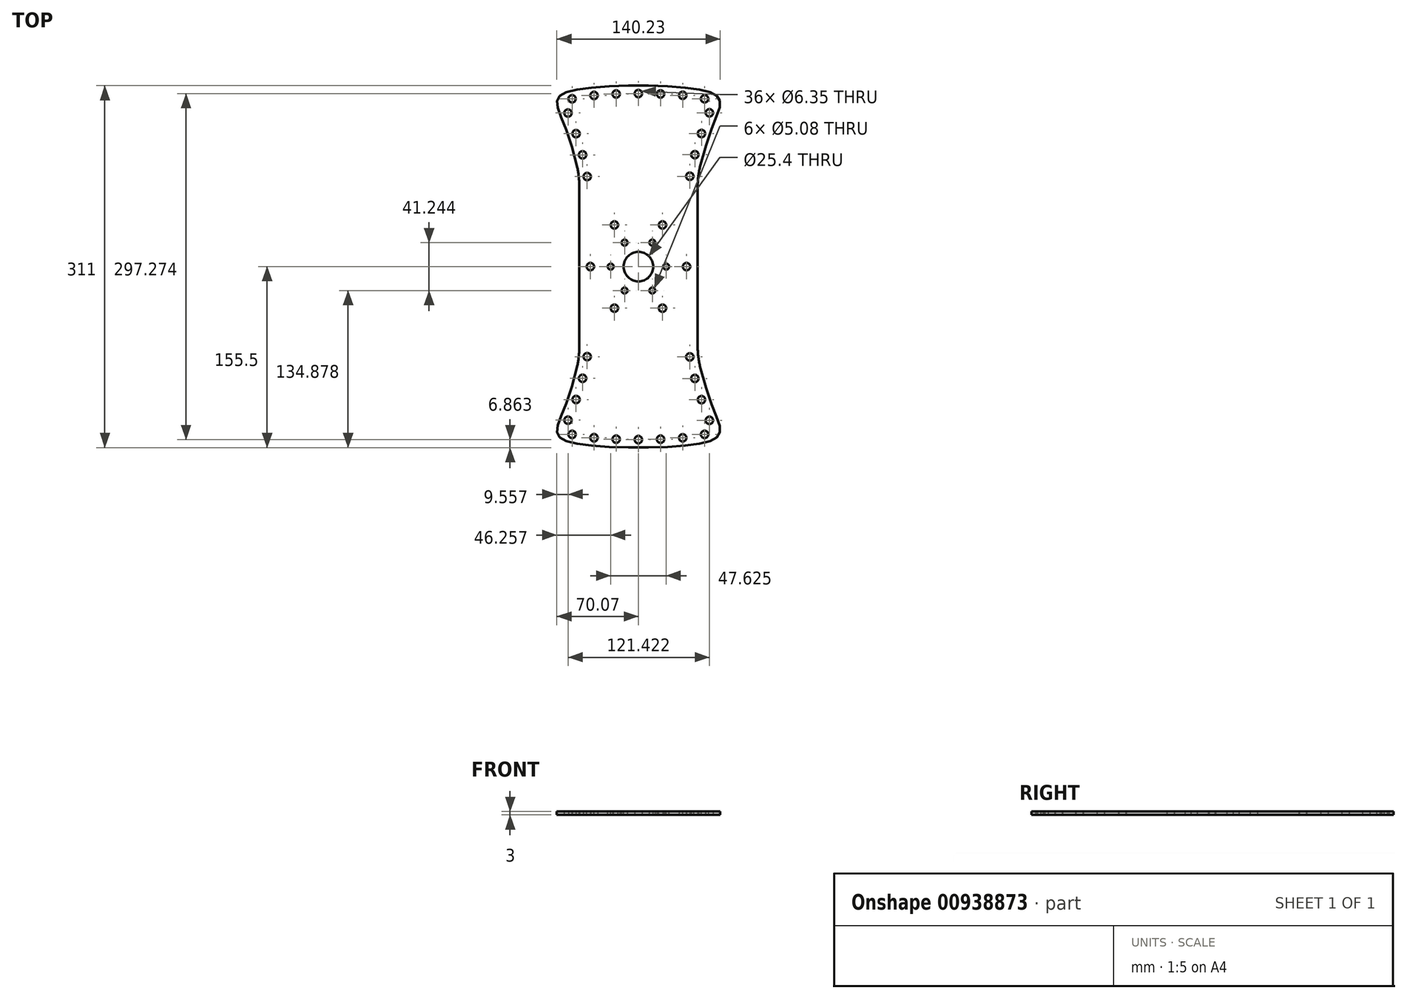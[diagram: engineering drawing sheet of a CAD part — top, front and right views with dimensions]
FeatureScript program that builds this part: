
annotation { "Feature Type Name" : "Feature", "Feature Type Description" : "" }
export const myFeature = defineFeature(function(context is Context, id is Id, definition is map)
    precondition{}
    {
        {
            var Q0;
            Q0=qCreatedBy(makeId("Top.planeOp"),FACE);
            var sketch = newSketch(context, id + "F0", { "sketchPlane" : qUnion([Q0])});
            skArc(sketch, "E0", {"start": v(-50.8, 0) * mm, "mid": v(0, -50.8) * mm, "end": v(50.8, 0) * mm});
            skLineSegment(sketch, "E1", {"start": v(-50.8, 0) * mm, "end": v(-50.8, 69.13) * mm});
            skLineSegment(sketch, "E2", {"start": v(50.8, 0) * mm, "end": v(50.8, 68.08) * mm});
            skFitSpline(sketch, "E3", {"points": [v(-50.8, 76.2) * mm, v(-69.85, 142.88) * mm, v(-50.8, 152.4) * mm, v(50.8, 152.4) * mm, v(69.85, 142.88) * mm, v(50.8, 76.2) * mm], "startDerivative": vector(-90.93, 536.28) * mm, "endDerivative": vector(-110.86, -555.74) * mm});
            skFitSpline(sketch, "E4.0", {"points": [v(-44.04, 77.35) * mm, v(-45.01, 83.1) * mm, v(-47.24, 93.68) * mm, v(-51.03, 107.03) * mm, v(-54.92, 118.08) * mm, v(-57.9, 125.53) * mm, v(-59.94, 130.5) * mm, v(-61.23, 133.73) * mm, v(-62.23, 136.46) * mm, v(-62.9, 138.66) * mm, v(-63.15, 139.98) * mm, v(-63.22, 140.7) * mm, v(-63.22, 141.05) * mm, v(-63.2, 141.23) * mm, v(-63.18, 141.28) * mm, v(-63.18, 141.28) * mm, v(-63.17, 141.3) * mm, v(-63.13, 141.35) * mm, v(-62.98, 141.54) * mm, v(-62.48, 141.96) * mm, v(-61.24, 142.67) * mm, v(-59.33, 143.45) * mm, v(-56.79, 144.22) * mm, v(-53.64, 144.94) * mm, v(-49.93, 145.62) * mm, v(-45.67, 146.24) * mm, v(-40.94, 146.79) * mm, v(-34.1, 147.44) * mm, v(-24.7, 148.07) * mm, v(-12.54, 148.53) * mm, v(0.06, 148.69) * mm, v(12.66, 148.54) * mm, v(24.8, 148.1) * mm, v(34.17, 147.47) * mm, v(40.97, 146.82) * mm, v(45.67, 146.25) * mm, v(49.9, 145.62) * mm, v(53.57, 144.93) * mm, v(56.68, 144.19) * mm, v(59.2, 143.4) * mm, v(61.1, 142.6) * mm, v(62.38, 141.88) * mm, v(62.93, 141.42) * mm, v(63.14, 141.19) * mm, v(63.21, 141.08) * mm, v(63.24, 141.03) * mm, v(63.25, 141) * mm, v(63.27, 140.95) * mm, v(63.3, 140.8) * mm, v(63.3, 140.5) * mm, v(63.28, 139.88) * mm, v(63.1, 138.7) * mm, v(62.54, 136.65) * mm, v(61.65, 134.06) * mm, v(60.48, 130.96) * mm, v(58.57, 126.14) * mm, v(55.7, 118.82) * mm, v(51.8, 107.8) * mm, v(47.79, 94.3) * mm, v(45.26, 83.47) * mm, v(44.07, 77.54) * mm]});
            skCircle(sketch, "E5", {"center": v(-56.97, 144.13) * mm, "radius": 3.18 * mm});
            skCircle(sketch, "E6", {"center": v(-38.15, 147.05) * mm, "radius": 3.18 * mm});
            skCircle(sketch, "E7", {"center": v(-19.13, 148.26) * mm, "radius": 3.18 * mm});
            skCircle(sketch, "E8", {"center": v(-0.08, 148.64) * mm, "radius": 3.18 * mm});
            skCircle(sketch, "E9", {"center": v(18.96, 148.3) * mm, "radius": 3.18 * mm});
            skCircle(sketch, "E10", {"center": v(37.98, 147.1) * mm, "radius": 3.18 * mm});
            skCircle(sketch, "E11", {"center": v(56.8, 144.12) * mm, "radius": 3.18 * mm});
            skCircle(sketch, "E12", {"center": v(-60.51, 131.94) * mm, "radius": 3.18 * mm});
            skCircle(sketch, "E13", {"center": v(-53.58, 114.2) * mm, "radius": 3.18 * mm});
            skCircle(sketch, "E14", {"center": v(-48, 95.98) * mm, "radius": 3.18 * mm});
            skCircle(sketch, "E15", {"center": v(-44.04, 77.35) * mm, "radius": 3.18 * mm});
            skCircle(sketch, "E16", {"center": v(60.9, 132.1) * mm, "radius": 3.18 * mm});
            skCircle(sketch, "E17", {"center": v(54.12, 114.31) * mm, "radius": 3.18 * mm});
            skCircle(sketch, "E18", {"center": v(48.43, 96.13) * mm, "radius": 3.18 * mm});
            skCircle(sketch, "E19", {"center": v(44.08, 77.58) * mm, "radius": 3.18 * mm});
            skArc(sketch, "E20.filletArc", {"start": v(52.82, 85.51) * mm, "mid": v(51.3, 76.86) * mm, "end": v(50.8, 68.08) * mm});
            skArc(sketch, "E21.filletArc", {"start": v(-50.8, 69.13) * mm, "mid": v(-51.2, 76.98) * mm, "end": v(-52.42, 84.75) * mm});
            skSolve(sketch);
        }
        {
            var Q0;
            Q0=makeQuery(id+"F0.imprint","IMPRINT",FACE,{"disambiguationData":[TD([[makeQuery(id+"F0.imprint","IMPRINT",EDGE,{"derivedFrom":sQuery(id+"F0.wireOp",EDGE,"E0")}),1.0]])]});
            extrude(context, id + "F1", {"entities" : qUnion([Q0]), "depth" : 3 * mm, "offsetDistance" : 25.4 * mm});
        }
        {
            var Q0;
            Q0=makeQuery(id+"F1.opExtrude","CAP_FACE",FACE,{"disambiguationData":[OSD([sQuery(id+"F0.wireOp",EDGE,"E0"),sQuery(id+"F0.wireOp",EDGE,"E1"),sQuery(id+"F0.wireOp",EDGE,"E2"),sQuery(id+"F0.wireOp",EDGE,"E3")])],"isStart":false});
            var sketch = newSketch(context, id + "F2", { "sketchPlane" : qUnion([Q0])});
            skCircle(sketch, "E22", {"center": v(0, 0) * mm, "radius": 23.81 * mm, "construction": true});
            skCircle(sketch, "E23", {"center": v(23.81, 0) * mm, "radius": 2.54 * mm});
            skCircle(sketch, "E24.1.0", {"center": v(11.9, 20.62) * mm, "radius": 2.54 * mm});
            skCircle(sketch, "E24.2.0", {"center": v(-11.9, 20.62) * mm, "radius": 2.54 * mm});
            skCircle(sketch, "E25.1.3.0", {"center": v(-23.81, 0) * mm, "radius": 2.54 * mm});
            skCircle(sketch, "E25.1.4.0", {"center": v(-11.9, -20.62) * mm, "radius": 2.54 * mm});
            skCircle(sketch, "E25.1.5.0", {"center": v(11.9, -20.62) * mm, "radius": 2.54 * mm});
            skCircle(sketch, "E26", {"center": v(0, 0) * mm, "radius": 12.7 * mm});
            skSolve(sketch);
        }
        {
            var Q0;
            Q0=makeQuery(id+"F2.imprint","IMPRINT",FACE,{"disambiguationData":[TD([[makeQuery(id+"F2.imprint","IMPRINT",EDGE,{"derivedFrom":sQuery(id+"F2.wireOp",EDGE,"E23")}),1.0]])]});
            var Q1;
            Q1=makeQuery(id+"F2.imprint","IMPRINT",FACE,{"disambiguationData":[TD([[makeQuery(id+"F2.imprint","IMPRINT",EDGE,{"derivedFrom":sQuery(id+"F2.wireOp",EDGE,"E24.1.0")}),1.0]])]});
            var Q2;
            Q2=makeQuery(id+"F2.imprint","IMPRINT",FACE,{"disambiguationData":[TD([[makeQuery(id+"F2.imprint","IMPRINT",EDGE,{"derivedFrom":sQuery(id+"F2.wireOp",EDGE,"E25.1.3.0")}),1.0]])]});
            var Q3;
            Q3=makeQuery(id+"F2.imprint","IMPRINT",FACE,{"disambiguationData":[TD([[makeQuery(id+"F2.imprint","IMPRINT",EDGE,{"derivedFrom":sQuery(id+"F2.wireOp",EDGE,"E25.1.4.0")}),1.0]])]});
            var Q4;
            Q4=makeQuery(id+"F2.imprint","IMPRINT",FACE,{"disambiguationData":[TD([[makeQuery(id+"F2.imprint","IMPRINT",EDGE,{"derivedFrom":sQuery(id+"F2.wireOp",EDGE,"E25.1.5.0")}),1.0]])]});
            var Q5;
            Q5=makeQuery(id+"F2.imprint","IMPRINT",FACE,{"disambiguationData":[TD([[makeQuery(id+"F2.imprint","IMPRINT",EDGE,{"derivedFrom":sQuery(id+"F2.wireOp",EDGE,"1dc40c13-e0c0-41ed-9b4d-84a6c58aea01.0")}),-1.0]])]});
            var Q6;
            Q6=makeQuery(id+"F2.imprint","IMPRINT",FACE,{"disambiguationData":[TD([[makeQuery(id+"F2.imprint","IMPRINT",EDGE,{"derivedFrom":sQuery(id+"F2.wireOp",EDGE,"E24.2.0")}),1.0]])]});
            var Q7;
            Q7=makeQuery(id+"F2.imprint","IMPRINT",FACE,{"disambiguationData":[TD([[makeQuery(id+"F2.imprint","IMPRINT",EDGE,{"derivedFrom":sQuery(id+"F2.wireOp",EDGE,"E26")}),1.0]])]});
            extrude(context, id + "F3", {"entities" : qUnion([Q0, Q1, Q2, Q3, Q4, Q5, Q6, Q7]), "operationType" : NewBodyOperationType.REMOVE, "endBound" : BoundingType.THROUGH_ALL, "oppositeDirection" : true, "depth" : 25.4 * mm, "offsetDistance" : 25.4 * mm});
        }
        {
            var Q0;
            Q0=makeQuery(id+"F1.opExtrude","CAP_FACE",FACE,{"disambiguationData":[OSD([sQuery(id+"F0.wireOp",EDGE,"E0"),sQuery(id+"F0.wireOp",EDGE,"E1"),sQuery(id+"F0.wireOp",EDGE,"E2"),sQuery(id+"F0.wireOp",EDGE,"E3")])],"isStart":false});
            var sketch = newSketch(context, id + "F4", { "sketchPlane" : qUnion([Q0])});
            skCircle(sketch, "E27", {"center": v(0, 0) * mm, "radius": 41.28 * mm, "construction": true});
            skCircle(sketch, "E28", {"center": v(41.28, 0) * mm, "radius": 3.18 * mm});
            skCircle(sketch, "E29.1.0", {"center": v(20.64, 35.75) * mm, "radius": 3.18 * mm});
            skCircle(sketch, "E29.2.0", {"center": v(-20.64, 35.75) * mm, "radius": 3.18 * mm});
            skCircle(sketch, "E29.3.0", {"center": v(-41.28, 0) * mm, "radius": 3.18 * mm});
            skCircle(sketch, "E29.4.0", {"center": v(-20.64, -35.75) * mm, "radius": 3.18 * mm});
            skCircle(sketch, "E29.5.0", {"center": v(20.64, -35.75) * mm, "radius": 3.18 * mm});
            skPoint(sketch, "E30", {"position": v(23.81, 0) * mm});
            skSolve(sketch);
        }
        {
            var Q0;
            Q0=makeQuery(id+"F4.imprint","IMPRINT",FACE,{"disambiguationData":[TD([[makeQuery(id+"F4.imprint","IMPRINT",EDGE,{"derivedFrom":sQuery(id+"F4.wireOp",EDGE,"E29.2.0")}),1.0]])]});
            var Q1;
            Q1=makeQuery(id+"F4.imprint","IMPRINT",FACE,{"disambiguationData":[TD([[makeQuery(id+"F4.imprint","IMPRINT",EDGE,{"derivedFrom":sQuery(id+"F4.wireOp",EDGE,"E29.3.0")}),1.0]])]});
            var Q2;
            Q2=makeQuery(id+"F4.imprint","IMPRINT",FACE,{"disambiguationData":[TD([[makeQuery(id+"F4.imprint","IMPRINT",EDGE,{"derivedFrom":sQuery(id+"F4.wireOp",EDGE,"E29.4.0")}),1.0]])]});
            var Q3;
            Q3=makeQuery(id+"F4.imprint","IMPRINT",FACE,{"disambiguationData":[TD([[makeQuery(id+"F4.imprint","IMPRINT",EDGE,{"derivedFrom":sQuery(id+"F4.wireOp",EDGE,"E29.5.0")}),1.0]])]});
            var Q4;
            Q4=makeQuery(id+"F4.imprint","IMPRINT",FACE,{"disambiguationData":[TD([[makeQuery(id+"F4.imprint","IMPRINT",EDGE,{"derivedFrom":sQuery(id+"F4.wireOp",EDGE,"E28")}),1.0]])]});
            var Q5;
            Q5=makeQuery(id+"F4.imprint","IMPRINT",FACE,{"disambiguationData":[TD([[makeQuery(id+"F4.imprint","IMPRINT",EDGE,{"derivedFrom":sQuery(id+"F4.wireOp",EDGE,"E29.1.0")}),1.0]])]});
            extrude(context, id + "F5", {"entities" : qUnion([Q0, Q1, Q2, Q3, Q4, Q5]), "operationType" : NewBodyOperationType.REMOVE, "endBound" : BoundingType.THROUGH_ALL, "oppositeDirection" : true, "depth" : 25.4 * mm, "offsetDistance" : 25.4 * mm});
        }
        {
            var Q0;
            Q0=makeQuery(id+"F1.opExtrude","SWEPT_BODY",BODY,{"disambiguationData":[OSD([sQuery(id+"F0.wireOp",EDGE,"E0"),sQuery(id+"F0.wireOp",EDGE,"E1"),sQuery(id+"F0.wireOp",EDGE,"E2"),sQuery(id+"F0.wireOp",EDGE,"E3"),sQuery(id+"F0.wireOp",EDGE,"E5"),sQuery(id+"F0.wireOp",EDGE,"E6"),sQuery(id+"F0.wireOp",EDGE,"E7"),sQuery(id+"F0.wireOp",EDGE,"E8"),sQuery(id+"F0.wireOp",EDGE,"E9"),sQuery(id+"F0.wireOp",EDGE,"E10"),sQuery(id+"F0.wireOp",EDGE,"E11"),sQuery(id+"F0.wireOp",EDGE,"E12"),sQuery(id+"F0.wireOp",EDGE,"E13"),sQuery(id+"F0.wireOp",EDGE,"E14"),sQuery(id+"F0.wireOp",EDGE,"E15"),sQuery(id+"F0.wireOp",EDGE,"E16"),sQuery(id+"F0.wireOp",EDGE,"E17"),sQuery(id+"F0.wireOp",EDGE,"E18"),sQuery(id+"F0.wireOp",EDGE,"E19"),sQuery(id+"F0.wireOp",EDGE,"E20.filletArc"),sQuery(id+"F0.wireOp",EDGE,"E21.filletArc")])]});
            var Q1;
            Q1=qCreatedBy(makeId("Front.planeOp"),FACE);
            mirror(context, id + "F6", {"operationType" : NewBodyOperationType.ADD, "entities" : qUnion([Q0]), "mirrorPlane" : qUnion([Q1])});
        }
    });
